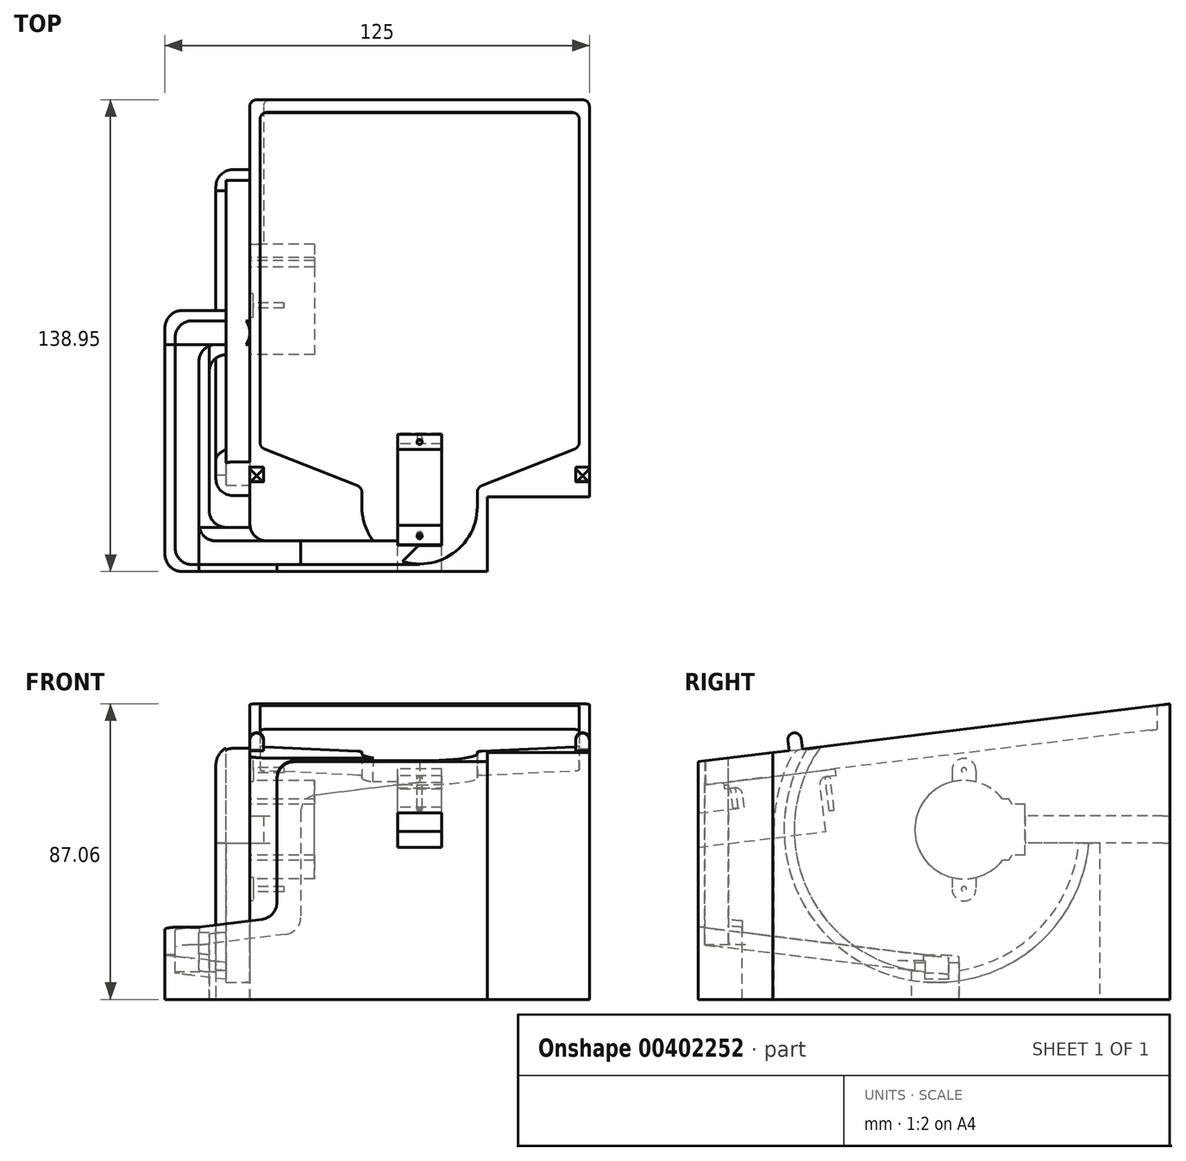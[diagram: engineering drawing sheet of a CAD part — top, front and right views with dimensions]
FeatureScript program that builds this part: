
annotation { "Feature Type Name" : "Feature", "Feature Type Description" : "" }
export const myFeature = defineFeature(function(context is Context, id is Id, definition is map)
    precondition{}
    {
        {
            var Q0;
            Q0=qCreatedBy(makeId("Right.planeOp"),FACE);
            var sketch = newSketch(context, id + "F0", { "sketchPlane" : qUnion([Q0])});
            skLineSegment(sketch, "E0", {"start": v(-65.34, 50) * mm, "end": v(-65.34, -20) * mm});
            skLineSegment(sketch, "E1", {"start": v(-65.34, -20) * mm, "end": v(73.61, -20) * mm});
            skLineSegment(sketch, "E2", {"start": v(73.61, -20) * mm, "end": v(73.61, 67.06) * mm});
            skLineSegment(sketch, "E3", {"start": v(73.61, 67.06) * mm, "end": v(-65.34, 50) * mm});
            skPoint(sketch, "E4", {"position": v(0, 58.02) * mm});
            skPoint(sketch, "E5", {"position": v(0, 50.97) * mm});
            skSolve(sketch);
        }
        {
            var Q0;
            Q0=qSketchRegion(id+"F0",true);
            extrude(context, id + "F1", {"entities" : qUnion([Q0]), "depth" : 50 * mm, "hasSecondDirection" : true, "secondDirectionOppositeDirection" : true, "secondDirectionDepth" : 50 * mm});
        }
        {
            var Q0;
            Q0=makeQuery(id+"F1.opExtrude","SWEPT_FACE",FACE,{"disambiguationData":[OSD([sQuery(id+"F0.wireOp",EDGE,"E3")])]});
            var sketch = newSketch(context, id + "F2", { "sketchPlane" : qUnion([Q0])});
            skPoint(sketch, "E6.endSnap0", {"position": v(0, -57.54) * mm});
            skPoint(sketch, "E6.end.orphan", {"position": v(0, -83) * mm});
            skPoint(sketch, "E7.orphan", {"position": v(-48, -57.54) * mm});
            skPoint(sketch, "E8.orphan", {"position": v(48, -57.54) * mm});
            skLineSegment(sketch, "E9.0", {"start": v(47, 77.46) * mm, "end": v(-47, 77.46) * mm});
            skLineSegment(sketch, "E9.1", {"start": v(47, 77.46) * mm, "end": v(47, -21.86) * mm});
            skLineSegment(sketch, "E9.2", {"start": v(-47, 77.46) * mm, "end": v(-47, -21.86) * mm});
            skLineSegment(sketch, "E9.3", {"start": v(17, -33.86) * mm, "end": v(47, -21.86) * mm});
            skLineSegment(sketch, "E9.4", {"start": v(-17, -33.86) * mm, "end": v(-47, -21.86) * mm});
            skLineSegment(sketch, "E9.5", {"start": v(-17, -39.54) * mm, "end": v(-17, -33.86) * mm});
            skArc(sketch, "E9.6", {"start": v(-17, -39.54) * mm, "mid": v(0, -56.54) * mm, "end": v(17, -39.54) * mm});
            skLineSegment(sketch, "E9.7", {"start": v(17, -39.54) * mm, "end": v(17, -33.86) * mm});
            skPoint(sketch, "E10.bottom.end.orphan", {"position": v(-48, 78.46) * mm});
            skPoint(sketch, "E10.bottom.start.orphan", {"position": v(48, 78.46) * mm});
            skPoint(sketch, "E11", {"position": v(0, 7.07) * mm});
            skSolve(sketch);
        }
        {
            var Q0;
            Q0=makeQuery(id+"F2.imprint","IMPRINT",FACE,{"disambiguationData":[TD([[makeQuery(id+"F2.imprint","IMPRINT",EDGE,{"derivedFrom":sQuery(id+"F2.wireOp",EDGE,"E9.0")}),1.0]])]});
            cPlane(context, id + "F3", {"entities" : qUnion([Q0]), "cplaneType" : CPlaneType.OFFSET, "offset" : 7 * mm, "oppositeDirection" : true, "width" : 150 * mm, "height" : 150 * mm});
        }
        {
            var Q0;
            Q0=qCreatedBy(id+"F3.planeOp",FACE);
            var sketch = newSketch(context, id + "F4", { "sketchPlane" : qUnion([Q0])});
            skPoint(sketch, "E12", {"position": v(0, 6.21) * mm});
            skPoint(sketch, "E13.endSnap0", {"position": v(0, -58.41) * mm});
            skPoint(sketch, "E13.end.orphan", {"position": v(0, -83.88) * mm});
            skPoint(sketch, "E14.orphan", {"position": v(-48, -58.41) * mm});
            skPoint(sketch, "E15.orphan", {"position": v(48, -58.41) * mm});
            skLineSegment(sketch, "E16.0", {"start": v(47, 76.59) * mm, "end": v(-47, 76.59) * mm});
            skLineSegment(sketch, "E16.1", {"start": v(47, 76.59) * mm, "end": v(47, -22.73) * mm});
            skLineSegment(sketch, "E16.2", {"start": v(-47, 76.59) * mm, "end": v(-47, -22.73) * mm});
            skLineSegment(sketch, "E16.3", {"start": v(17, -34.73) * mm, "end": v(47, -22.73) * mm});
            skLineSegment(sketch, "E16.4", {"start": v(-17, -34.73) * mm, "end": v(-47, -22.73) * mm});
            skLineSegment(sketch, "E16.5", {"start": v(-17, -40.41) * mm, "end": v(-17, -34.73) * mm});
            skArc(sketch, "E16.6", {"start": v(-17, -40.41) * mm, "mid": v(0, -57.41) * mm, "end": v(17, -40.41) * mm});
            skLineSegment(sketch, "E16.7", {"start": v(17, -40.41) * mm, "end": v(17, -34.73) * mm});
            skPoint(sketch, "E17.bottom.end.orphan", {"position": v(-48, 77.59) * mm});
            skPoint(sketch, "E17.bottom.start.orphan", {"position": v(48, 77.59) * mm});
            skSolve(sketch);
        }
        {
            var Q1;
            Q1 = qSketchRegion(id + "F2", true);
            var Q2;
            Q2 = qSketchRegion(id + "F4", true);
            loft(context, id + "F5", {"operationType" : NewBodyOperationType.REMOVE, "sheetProfilesArray" : [{ "sheetProfileEntities" : qUnion([Q1]) }, { "sheetProfileEntities" : qUnion([Q2]) }]});
        }
        {
            var Q0;
            Q0=makeQuery(id+"F1.opExtrude","CAP_FACE",FACE,{"disambiguationData":[OSD([sQuery(id+"F0.wireOp",EDGE,"E0"),sQuery(id+"F0.wireOp",EDGE,"E1"),sQuery(id+"F0.wireOp",EDGE,"E2"),sQuery(id+"F0.wireOp",EDGE,"E3")])],"isStart":true});
            var sketch = newSketch(context, id + "F6", { "sketchPlane" : qUnion([Q0])});
            skArc(sketch, "E18", {"start": v(-24.37, 21) * mm, "mid": v(1.5, 30) * mm, "end": v(-24.37, 39) * mm});
            skPoint(sketch, "E19", {"position": v(-5, 30) * mm});
            skLineSegment(sketch, "E20.bottom", {"start": v(-31, 22.5) * mm, "end": v(-27.13, 22.5) * mm});
            skLineSegment(sketch, "E20.top", {"start": v(-31, 37.5) * mm, "end": v(-27.13, 37.5) * mm});
            skLineSegment(sketch, "E20.left", {"start": v(-31, 22.5) * mm, "end": v(-31, 37.5) * mm});
            skArc(sketch, "E21", {"start": v(-26.23, 39) * mm, "mid": v(-26.7, 38.26) * mm, "end": v(-27.13, 37.5) * mm});
            skLineSegment(sketch, "E22.bottom", {"start": v(-26.23, 39) * mm, "end": v(-24.37, 39) * mm});
            skLineSegment(sketch, "E22.top", {"start": v(-26.23, 21) * mm, "end": v(-24.37, 21) * mm});
            skArc(sketch, "E23.trimOffspring", {"start": v(-27.13, 22.5) * mm, "mid": v(-26.7, 21.74) * mm, "end": v(-26.23, 21) * mm});
            skSolve(sketch);
        }
        {
            var Q0;
            Q0 = qSketchRegion(id + "F6", true);
            extrude(context, id + "F7", {"entities" : qUnion([Q0]), "operationType" : NewBodyOperationType.REMOVE, "oppositeDirection" : true, "depth" : 19 * mm});
        }
        {
            var Q0;
            Q0=makeQuery(id+"F1.opExtrude","CAP_FACE",FACE,{"disambiguationData":[OSD([sQuery(id+"F0.wireOp",EDGE,"E0"),sQuery(id+"F0.wireOp",EDGE,"E1"),sQuery(id+"F0.wireOp",EDGE,"E2"),sQuery(id+"F0.wireOp",EDGE,"E3")])],"isStart":true});
            var sketch = newSketch(context, id + "F8", { "sketchPlane" : qUnion([Q0])});
            skLineSegment(sketch, "E24", {"start": v(-13, 47.5) * mm, "end": v(-13, 12.5) * mm});
            skPoint(sketch, "E25", {"position": v(-13, 30) * mm});
            skArc(sketch, "E26.0.startCap", {"start": v(-16.5, 47.5) * mm, "mid": v(-13, 51) * mm, "end": v(-9.5, 47.5) * mm});
            skArc(sketch, "E26.0.endCap", {"start": v(-9.5, 12.5) * mm, "mid": v(-13, 9) * mm, "end": v(-16.5, 12.5) * mm});
            skLineSegment(sketch, "E26.0.left", {"start": v(-9.5, 47.5) * mm, "end": v(-9.5, 12.5) * mm});
            skLineSegment(sketch, "E26.0.right", {"start": v(-16.5, 47.5) * mm, "end": v(-16.5, 12.5) * mm});
            skSolve(sketch);
        }
        {
            var Q0;
            Q0 = qSketchRegion(id + "F8", true);
            extrude(context, id + "F9", {"entities" : qUnion([Q0]), "operationType" : NewBodyOperationType.REMOVE, "oppositeDirection" : true, "depth" : 1 * mm});
        }
        {
            var Q0;
            Q0=makeQuery(id+"F1.opExtrude","CAP_FACE",FACE,{"disambiguationData":[OSD([sQuery(id+"F0.wireOp",EDGE,"E0"),sQuery(id+"F0.wireOp",EDGE,"E1"),sQuery(id+"F0.wireOp",EDGE,"E2"),sQuery(id+"F0.wireOp",EDGE,"E3")])],"isStart":true});
            var sketch = newSketch(context, id + "F10", { "sketchPlane" : qUnion([Q0])});
            skLineSegment(sketch, "E27.bottom", {"start": v(-81, 34) * mm, "end": v(-21, 34) * mm});
            skLineSegment(sketch, "E27.top", {"start": v(-81, 26) * mm, "end": v(-21, 26) * mm});
            skLineSegment(sketch, "E27.left", {"start": v(-81, 34) * mm, "end": v(-81, 26) * mm});
            skLineSegment(sketch, "E27.right", {"start": v(-21, 34) * mm, "end": v(-21, 26) * mm});
            skPoint(sketch, "E27.middle", {"position": v(-51, 30) * mm});
            skSolve(sketch);
        }
        {
            var Q0;
            Q0 = qSketchRegion(id + "F10", true);
            extrude(context, id + "F11", {"entities" : qUnion([Q0]), "operationType" : NewBodyOperationType.REMOVE, "oppositeDirection" : true, "depth" : 4 * mm});
        }
        {
            var Q0;
            Q0=qCreatedBy(makeId("Front.planeOp"),FACE);
            cPlane(context, id + "F12", {"entities" : qUnion([Q0]), "cplaneType" : CPlaneType.OFFSET, "offset" : 5 * mm, "oppositeDirection" : true, "width" : 150 * mm, "height" : 150 * mm});
        }
        {
            var Q0;
            Q0=qCreatedBy(id+"F12.planeOp",FACE);
            var sketch = newSketch(context, id + "F13", { "sketchPlane" : qUnion([Q0])});
            skLineSegment(sketch, "E28", {"start": v(-50, -20) * mm, "end": v(-75, -20) * mm});
            skLineSegment(sketch, "E29", {"start": v(-50, -9.96) * mm, "end": v(-75, -6.9) * mm});
            skLineSegment(sketch, "E30", {"start": v(-75, -20) * mm, "end": v(-75, -6.9) * mm});
            skLineSegment(sketch, "E31", {"start": v(-50, -20) * mm, "end": v(-50, -9.96) * mm});
            skSolve(sketch);
        }
        {
            var Q0;
            Q0 = qSketchRegion(id + "F13", true);
            extrude(context, id + "F14", {"entities" : qUnion([Q0]), "operationType" : NewBodyOperationType.ADD, "depth" : 6.5 * mm, "hasSecondDirection" : true, "secondDirectionOppositeDirection" : true, "secondDirectionDepth" : 6.5 * mm});
        }
        {
            var Q0;
            Q0=makeQuery(id+"F2.imprint","IMPRINT",FACE,{"disambiguationData":[TD([[makeQuery(id+"F2.imprint","IMPRINT",EDGE,{"derivedFrom":sQuery(id+"F2.wireOp",EDGE,"E9.0")}),1.0]])]});
            var sketch = newSketch(context, id + "F15", { "sketchPlane" : qUnion([Q0])});
            skLineSegment(sketch, "E32.bottom", {"start": v(6.5, -46.91) * mm, "end": v(-6.5, -46.91) * mm});
            skLineSegment(sketch, "E32.top", {"start": v(6.5, -23.91) * mm, "end": v(-6.5, -23.91) * mm});
            skLineSegment(sketch, "E32.left", {"start": v(6.5, -46.91) * mm, "end": v(6.5, -23.91) * mm});
            skLineSegment(sketch, "E32.right", {"start": v(-6.5, -46.91) * mm, "end": v(-6.5, -23.91) * mm});
            skPoint(sketch, "E32.middle", {"position": v(0, -35.41) * mm});
            skSolve(sketch);
        }
        {
            var Q0;
            Q0 = qSketchRegion(id + "F15", true);
            extrude(context, id + "F16", {"entities" : qUnion([Q0]), "operationType" : NewBodyOperationType.REMOVE, "oppositeDirection" : true, "depth" : 25 * mm});
        }
        {
            var Q0;
            Q0=makeQuery(id+"F2.imprint","IMPRINT",FACE,{"disambiguationData":[TD([[makeQuery(id+"F2.imprint","IMPRINT",EDGE,{"derivedFrom":sQuery(id+"F2.wireOp",EDGE,"E9.0")}),1.0]])]});
            var sketch = newSketch(context, id + "F17", { "sketchPlane" : qUnion([Q0])});
            skLineSegment(sketch, "E33.bottom", {"start": v(6.5, -18.91) * mm, "end": v(-6.5, -18.91) * mm});
            skLineSegment(sketch, "E33.top", {"start": v(6.5, -51.91) * mm, "end": v(-6.5, -51.91) * mm});
            skLineSegment(sketch, "E33.left", {"start": v(6.5, -18.91) * mm, "end": v(6.5, -51.91) * mm});
            skLineSegment(sketch, "E33.right", {"start": v(-6.5, -18.91) * mm, "end": v(-6.5, -51.91) * mm});
            skPoint(sketch, "E33.middle", {"position": v(0, -35.41) * mm});
            skSolve(sketch);
        }
        {
            var Q0;
            Q0 = qSketchRegion(id + "F17", true);
            extrude(context, id + "F18", {"entities" : qUnion([Q0]), "operationType" : NewBodyOperationType.REMOVE, "oppositeDirection" : true, "depth" : 9 * mm});
        }
        {
            var Q0;
            Q0=makeQuery(id+"FUqeBeKpT4LYNuk_1.boolean.opBoolean","MERGE",FACE,{"derivedFrom":[makeQuery(id+"F1.opExtrude","SWEPT_FACE",FACE,{"disambiguationData":[OSD([sQuery(id+"F0.wireOp",EDGE,"E0")])]}),makeQuery(id+"F61UTTqEWsXgY2D_1.opExtrude","SWEPT_FACE",FACE,{"disambiguationData":[OSD([sQuery(id+"F9Du9WT9e9JY5Dl_1.wireOp",EDGE,"sJgd1tPc-9qsz-vVnT-TqeQ-4TYIqpoZbmCu")])]}),makeQuery(id+"FUqeBeKpT4LYNuk_1.opExtrude","CAP_FACE",FACE,{"disambiguationData":[OSD([sQuery(id+"Fu5qXJoa0auTo1w_1.wireOp",EDGE,"depduNjt-3aMR-BOii-vv3o-0Txvqa5xbjUM"),sQuery(id+"Fu5qXJoa0auTo1w_1.wireOp",EDGE,"YClS0oY7-eXia-WmQ4-NOUT-qmrgQAcRW2ul"),sQuery(id+"Fu5qXJoa0auTo1w_1.wireOp",EDGE,"FjPESpCu-MEkZ-X1k0-rLkk-jPPFp3MV8du9"),sQuery(id+"Fu5qXJoa0auTo1w_1.wireOp",EDGE,"T3NzeVoH-fv4R-7HJz-S144-zwuEIWOQCuFN")])],"isStart":true})]});
            var sketch = newSketch(context, id + "F19", { "sketchPlane" : qUnion([Q0])});
            skLineSegment(sketch, "E34.bottom", {"start": v(50, -20) * mm, "end": v(20, -20) * mm});
            skLineSegment(sketch, "E34.top", {"start": v(50, 60) * mm, "end": v(20, 60) * mm});
            skLineSegment(sketch, "E34.left", {"start": v(50, -20) * mm, "end": v(50, 60) * mm});
            skLineSegment(sketch, "E34.right", {"start": v(20, -20) * mm, "end": v(20, 60) * mm});
            skSolve(sketch);
        }
        {
            var Q0;
            Q0 = qSketchRegion(id + "F19", true);
            extrude(context, id + "F20", {"entities" : qUnion([Q0]), "operationType" : NewBodyOperationType.REMOVE, "oppositeDirection" : true, "depth" : 22 * mm});
        }
        {
            var Q0;
            Q0=makeQuery(id+"F16.boolean.opBoolean","COPY",FACE,{"derivedFrom":makeQuery(id+"F16.opExtrude","SWEPT_FACE",FACE,{"disambiguationData":[OSD([sQuery(id+"F15.wireOp",EDGE,"E32.bottom")])]})});
            var sketch = newSketch(context, id + "F21", { "sketchPlane" : qUnion([Q0])});
            skLineSegment(sketch, "E35.bottom", {"start": v(-6.5, 32.6) * mm, "end": v(6.5, 32.6) * mm});
            skLineSegment(sketch, "E35.top", {"start": v(-6.5, 42.6) * mm, "end": v(6.5, 42.6) * mm});
            skLineSegment(sketch, "E35.left", {"start": v(-6.5, 32.6) * mm, "end": v(-6.5, 42.6) * mm});
            skLineSegment(sketch, "E35.right", {"start": v(6.5, 32.6) * mm, "end": v(6.5, 42.6) * mm});
            skSolve(sketch);
        }
        {
            var Q0;
            Q0 = qSketchRegion(id + "F21", true);
            extrude(context, id + "F22", {"entities" : qUnion([Q0]), "operationType" : NewBodyOperationType.REMOVE, "oppositeDirection" : true, "depth" : 25 * mm});
        }
        {
            var Q0;
            Q0=qCreatedBy(id+"F12.planeOp",FACE);
            var sketch = newSketch(context, id + "F23", { "sketchPlane" : qUnion([Q0])});
            skLineSegment(sketch, "E36", {"start": v(-50, -6.3) * mm, "end": v(-50, -15) * mm});
            skLineSegment(sketch, "E37", {"start": v(-50, -15) * mm, "end": v(-72, -12.3) * mm});
            skLineSegment(sketch, "E38", {"start": v(-72, -12.3) * mm, "end": v(-72, -6.3) * mm});
            skLineSegment(sketch, "E39", {"start": v(-72, -6.3) * mm, "end": v(-50, -6.3) * mm});
            skSolve(sketch);
        }
        {
            var Q0;
            Q0 = qSketchRegion(id + "F23", true);
            extrude(context, id + "F24", {"entities" : qUnion([Q0]), "operationType" : NewBodyOperationType.REMOVE, "oppositeDirection" : true, "depth" : 3.5 * mm, "hasSecondDirection" : true, "secondDirectionOppositeDirection" : false, "secondDirectionDepth" : 3.5 * mm});
        }
        {
            var Q0;
            Q0=makeQuery(id+"F14.opExtrude","SWEPT_FACE",FACE,{"disambiguationData":[OSD([sQuery(id+"F13.wireOp",EDGE,"E30")])]});
            var sketch = newSketch(context, id + "F25", { "sketchPlane" : qUnion([Q0])});
            skLineSegment(sketch, "E40", {"start": v(1.5, -20) * mm, "end": v(65.34, -20) * mm});
            skLineSegment(sketch, "E41", {"start": v(65.34, -20) * mm, "end": v(65.34, 1.31) * mm});
            skLineSegment(sketch, "E42", {"start": v(65.34, 1.31) * mm, "end": v(-1.5, -6.9) * mm});
            skLineSegment(sketch, "E43", {"start": v(-1.5, -6.9) * mm, "end": v(-1.5, -20) * mm});
            skLineSegment(sketch, "E44", {"start": v(-1.5, -20) * mm, "end": v(1.5, -20) * mm});
            skSolve(sketch);
        }
        {
            var Q0;
            Q0 = qSketchRegion(id + "F25", true);
            extrude(context, id + "F26", {"entities" : qUnion([Q0]), "operationType" : NewBodyOperationType.ADD, "oppositeDirection" : true, "depth" : 13 * mm});
        }
        {
            var Q0;
            Q0=makeQuery(id+"F26.boolean.opBoolean","MERGE",FACE,{"derivedFrom":[makeQuery(id+"F14.opExtrude","SWEPT_FACE",FACE,{"disambiguationData":[OSD([sQuery(id+"F13.wireOp",EDGE,"E30")])]}),makeQuery(id+"F26.opExtrude","CAP_FACE",FACE,{"disambiguationData":[OSD([sQuery(id+"F25.wireOp",EDGE,"E40"),sQuery(id+"F25.wireOp",EDGE,"E41"),sQuery(id+"F25.wireOp",EDGE,"E42"),sQuery(id+"F25.wireOp",EDGE,"E43"),sQuery(id+"F25.wireOp",EDGE,"E44")])],"isStart":true})]});
            cPlane(context, id + "F27", {"entities" : qUnion([Q0]), "cplaneType" : CPlaneType.OFFSET, "offset" : 3 * mm, "oppositeDirection" : true, "width" : 150 * mm, "height" : 150 * mm});
        }
        {
            var Q0;
            Q0=qCreatedBy(id+"F27.planeOp",FACE);
            var sketch = newSketch(context, id + "F28", { "sketchPlane" : qUnion([Q0])});
            skLineSegment(sketch, "E45", {"start": v(-1.5, -2.4) * mm, "end": v(-1.5, -11.93) * mm});
            skLineSegment(sketch, "E46", {"start": v(-1.5, -11.93) * mm, "end": v(63.34, -3.97) * mm});
            skLineSegment(sketch, "E47", {"start": v(63.34, -3.97) * mm, "end": v(63.34, 3.33) * mm});
            skLineSegment(sketch, "E48", {"start": v(63.34, 3.33) * mm, "end": v(-1.5, 3.33) * mm});
            skLineSegment(sketch, "E49", {"start": v(-1.5, 3.33) * mm, "end": v(-1.5, -2.4) * mm});
            skSolve(sketch);
        }
        {
            var Q0;
            Q0 = qSketchRegion(id + "F28", true);
            extrude(context, id + "F29", {"entities" : qUnion([Q0]), "operationType" : NewBodyOperationType.REMOVE, "oppositeDirection" : true, "depth" : 7 * mm});
        }
        {
            var Q0;
            Q0=makeQuery(id+"F1.opExtrude","SWEPT_FACE",FACE,{"disambiguationData":[OSD([sQuery(id+"F0.wireOp",EDGE,"E0")])]});
            var sketch = newSketch(context, id + "F30", { "sketchPlane" : qUnion([Q0])});
            skLineSegment(sketch, "E50", {"start": v(-50, -20) * mm, "end": v(-50, 3.16) * mm});
            skLineSegment(sketch, "E51", {"start": v(-50, 3.16) * mm, "end": v(-65, 1.31) * mm});
            skLineSegment(sketch, "E52", {"start": v(-65, 1.31) * mm, "end": v(-65, -20) * mm});
            skLineSegment(sketch, "E53", {"start": v(-65, -20) * mm, "end": v(-50, -20) * mm});
            skSolve(sketch);
        }
        {
            var Q0;
            Q0 = qSketchRegion(id + "F30", true);
            extrude(context, id + "F31", {"entities" : qUnion([Q0]), "operationType" : NewBodyOperationType.ADD, "oppositeDirection" : true, "depth" : 13 * mm});
        }
        {
            var Q0;
            Q0=makeQuery(id+"F29.boolean.opBoolean","COPY",FACE,{"derivedFrom":makeQuery(id+"F29.opExtrude","SWEPT_FACE",FACE,{"disambiguationData":[OSD([sQuery(id+"F28.wireOp",EDGE,"E47")])]})});
            var sketch = newSketch(context, id + "F32", { "sketchPlane" : qUnion([Q0])});
            skLineSegment(sketch, "E54", {"start": v(65, -3.97) * mm, "end": v(65, 76.03) * mm});
            skLineSegment(sketch, "E55", {"start": v(65, 76.03) * mm, "end": v(0, 76.03) * mm});
            skLineSegment(sketch, "E56", {"start": v(0, 76.03) * mm, "end": v(0, 43.93) * mm});
            skLineSegment(sketch, "E57", {"start": v(0, 43.93) * mm, "end": v(35, 39.63) * mm});
            skLineSegment(sketch, "E58", {"start": v(35, 39.63) * mm, "end": v(35, -0.29) * mm});
            skLineSegment(sketch, "E59", {"start": v(35, -0.29) * mm, "end": v(65, -3.97) * mm});
            skSolve(sketch);
        }
        {
            var Q0;
            Q0 = qSketchRegion(id + "F32", true);
            extrude(context, id + "F33", {"entities" : qUnion([Q0]), "operationType" : NewBodyOperationType.REMOVE, "depth" : 7 * mm});
        }
        {
            var Q0;
            Q0=makeQuery(id+"F33.boolean.opBoolean","MERGE",FACE,{"derivedFrom":[makeQuery(id+"F29.boolean.opBoolean","COPY",FACE,{"derivedFrom":makeQuery(id+"F29.opExtrude","SWEPT_FACE",FACE,{"disambiguationData":[OSD([sQuery(id+"F28.wireOp",EDGE,"E47")])]})}),makeQuery(id+"F33.opExtrude","CAP_FACE",FACE,{"disambiguationData":[OSD([sQuery(id+"F32.wireOp",EDGE,"E54"),sQuery(id+"F32.wireOp",EDGE,"E55"),sQuery(id+"F32.wireOp",EDGE,"E56"),sQuery(id+"F32.wireOp",EDGE,"E57"),sQuery(id+"F32.wireOp",EDGE,"E58"),sQuery(id+"F32.wireOp",EDGE,"E59")])],"isStart":true})]});
            var sketch = newSketch(context, id + "F34", { "sketchPlane" : qUnion([Q0])});
            skLineSegment(sketch, "E60", {"start": v(50, 3.16) * mm, "end": v(42, 4.14) * mm});
            skLineSegment(sketch, "E61", {"start": v(42, 4.14) * mm, "end": v(42, 50.25) * mm});
            skLineSegment(sketch, "E62", {"start": v(42, 50.25) * mm, "end": v(50, 50.25) * mm});
            skLineSegment(sketch, "E63", {"start": v(50, 50.25) * mm, "end": v(50, 3.16) * mm});
            skSolve(sketch);
        }
        {
            var Q0;
            Q0 = qSketchRegion(id + "F34", true);
            extrude(context, id + "F35", {"entities" : qUnion([Q0]), "operationType" : NewBodyOperationType.REMOVE, "oppositeDirection" : true, "depth" : 3 * mm});
        }
        {
            var Q0;
            Q0=makeQuery(id+"F6.imprint","IMPRINT",FACE,{"disambiguationData":[TD([[makeQuery(id+"F6.imprint","IMPRINT",EDGE,{"derivedFrom":sQuery(id+"F6.wireOp",EDGE,"E18")}),-1.0]])]});
            var sketch = newSketch(context, id + "F36", { "sketchPlane" : qUnion([Q0])});
            skArc(sketch, "E64", {"start": v(-49.82, 26) * mm, "mid": v(-37.7, -0.92) * mm, "end": v(-11.5, -14.53) * mm});
            skArc(sketch, "E65", {"start": v(43, 30) * mm, "mid": v(41.44, 42.14) * mm, "end": v(36.86, 53.5) * mm});
            skLineSegment(sketch, "E66", {"start": v(36.86, 53.5) * mm, "end": v(33.1, 53.96) * mm});
            skPoint(sketch, "E67", {"position": v(43, 30) * mm});
            skLineSegment(sketch, "E68", {"start": v(43, 30) * mm, "end": v(43, -20) * mm});
            skLineSegment(sketch, "E69", {"start": v(-53, 26) * mm, "end": v(-53, -20) * mm});
            skLineSegment(sketch, "E70", {"start": v(-53, -20) * mm, "end": v(43, -20) * mm});
            skLineSegment(sketch, "E71", {"start": v(-53, 26) * mm, "end": v(-49.82, 26) * mm});
            skLineSegment(sketch, "E72", {"start": v(-11.5, -14.53) * mm, "end": v(-11.5, -20) * mm});
            skLineSegment(sketch, "E73", {"start": v(1.5, -14.53) * mm, "end": v(1.5, -20) * mm});
            skArc(sketch, "E74.trimOffspring", {"start": v(1.5, -14.53) * mm, "mid": v(35.86, 11.15) * mm, "end": v(33.1, 53.96) * mm});
            skSolve(sketch);
        }
        {
            var Q0;
            Q0 = qSketchRegion(id + "F36", true);
            extrude(context, id + "F37", {"entities" : qUnion([Q0]), "operationType" : NewBodyOperationType.ADD, "depth" : 10 * mm});
        }
        {
            var Q0;
            Q0=makeQuery(id+"F37.opExtrude","CAP_FACE",FACE,{"disambiguationData":[OSD([sQuery(id+"F36.wireOp",EDGE,"E64"),sQuery(id+"F36.wireOp",EDGE,"E69"),sQuery(id+"F36.wireOp",EDGE,"E70"),sQuery(id+"F36.wireOp",EDGE,"E71"),sQuery(id+"F36.wireOp",EDGE,"E72")])],"isStart":false});
            var sketch = newSketch(context, id + "F38", { "sketchPlane" : qUnion([Q0])});
            skArc(sketch, "E75", {"start": v(1.5, -14.53) * mm, "mid": v(35.86, 11.15) * mm, "end": v(33.1, 53.96) * mm});
            skArc(sketch, "E76", {"start": v(1.5, -11.5) * mm, "mid": v(33.73, 13.76) * mm, "end": v(29.15, 54.44) * mm});
            skLineSegment(sketch, "E77", {"start": v(-49.82, 26) * mm, "end": v(-46.8, 26) * mm});
            skLineSegment(sketch, "E78", {"start": v(33.1, 53.96) * mm, "end": v(29.15, 54.44) * mm});
            skLineSegment(sketch, "E79", {"start": v(-11.5, -14.53) * mm, "end": v(-11.5, -11.5) * mm});
            skLineSegment(sketch, "E80", {"start": v(1.5, -14.53) * mm, "end": v(1.5, -11.5) * mm});
            skArc(sketch, "E81.trimOffspring", {"start": v(-46.8, 26) * mm, "mid": v(-35.58, 1.2) * mm, "end": v(-11.5, -11.5) * mm});
            skArc(sketch, "E82.trimOffspring", {"start": v(-49.82, 26) * mm, "mid": v(-37.7, -0.92) * mm, "end": v(-11.5, -14.53) * mm});
            skSolve(sketch);
        }
        {
            var Q0;
            Q0 = qSketchRegion(id + "F38", true);
            extrude(context, id + "F39", {"entities" : qUnion([Q0]), "operationType" : NewBodyOperationType.ADD, "oppositeDirection" : true, "depth" : 3 * mm});
        }
        {
            var Q0;
            Q0=makeQuery(id+"F6.imprint","IMPRINT",FACE,{"disambiguationData":[TD([[makeQuery(id+"F6.imprint","IMPRINT",EDGE,{"derivedFrom":sQuery(id+"F6.wireOp",EDGE,"E18")}),-1.0]])]});
            var sketch = newSketch(context, id + "F40", { "sketchPlane" : qUnion([Q0])});
            skCircle(sketch, "E83", {"center": v(-5, 30) * mm, "radius": 45 * mm});
            skSolve(sketch);
        }
        {
            var Q0;
            Q0 = qSketchRegion(id + "F40", true);
            extrude(context, id + "F41", {"entities" : qUnion([Q0]), "operationType" : NewBodyOperationType.REMOVE, "depth" : 7 * mm});
        }
        {
            var Q0;
            Q0=makeQuery(id+"F20.boolean.opBoolean","COPY",EDGE,{"derivedFrom":makeQuery(id+"F20.opExtrude","CAP_EDGE",EDGE,{"disambiguationData":[OSD([sQuery(id+"F19.wireOp",EDGE,"E34.right")])],"isStart":true})});
            var Q1;
            Q1=makeQuery(id+"F20.boolean.opBoolean","COPY",EDGE,{"derivedFrom":makeQuery(id+"F20.opExtrude","CAP_EDGE",EDGE,{"disambiguationData":[OSD([sQuery(id+"F19.wireOp",EDGE,"E34.left")])],"isStart":false})});
            var Q2;
            Q2=makeQuery(id+"F37.opExtrude","CAP_EDGE",EDGE,{"disambiguationData":[OSD([sQuery(id+"F36.wireOp",EDGE,"E69")])],"isStart":false});
            var Q3;
            Q3=makeQuery(id+"F37.opExtrude","CAP_EDGE",EDGE,{"disambiguationData":[OSD([sQuery(id+"F36.wireOp",EDGE,"E68")])],"isStart":false});
            var Q4;
            Q4=makeQuery(id+"F37.opExtrude","SWEPT_EDGE",EDGE,{"disambiguationData":[OSD([sQuery(id+"F0.wireOp",EDGE,"E3"),sQuery(id+"F36.wireOp",EDGE,"E65"),sQuery(id+"F36.wireOp",EDGE,"E66")])]});
            var Q5;
            Q5=makeQuery(id+"F39.boolean.opBoolean","MERGE",EDGE,{"derivedFrom":[makeQuery(id+"F37.opExtrude","CAP_EDGE",EDGE,{"disambiguationData":[OSD([sQuery(id+"F36.wireOp",EDGE,"E66")])],"isStart":false}),makeQuery(id+"F39.opExtrude","CAP_EDGE",EDGE,{"disambiguationData":[OSD([sQuery(id+"F38.wireOp",EDGE,"E78")])],"isStart":true})]});
            var Q6;
            Q6=makeQuery(id+"F14.opExtrude","CAP_EDGE",EDGE,{"disambiguationData":[OSD([sQuery(id+"F13.wireOp",EDGE,"E30")])],"isStart":true});
            var Q7;
            Q7=makeQuery(id+"F26.opExtrude","CAP_EDGE",EDGE,{"disambiguationData":[OSD([sQuery(id+"F25.wireOp",EDGE,"E41")])],"isStart":true});
            var Q8;
            Q8=makeQuery(id+"F35.boolean.opBoolean","INTERSECT",EDGE,{"derivedFrom":[makeQuery(id+"F1.opExtrude","SWEPT_FACE",FACE,{"disambiguationData":[OSD([sQuery(id+"F0.wireOp",EDGE,"E3")])]}),makeQuery(id+"F35.opExtrude","SWEPT_FACE",FACE,{"disambiguationData":[OSD([sQuery(id+"F34.wireOp",EDGE,"E61")])]})]});
            var Q9;
            Q9=makeQuery(id+"F33.boolean.opBoolean","COPY",EDGE,{"derivedFrom":makeQuery(id+"F33.opExtrude","CAP_EDGE",EDGE,{"disambiguationData":[OSD([sQuery(id+"F32.wireOp",EDGE,"E54")])],"isStart":false})});
            var Q10;
            Q10=makeQuery(id+"F31.boolean.opBoolean","INTERSECT",EDGE,{"derivedFrom":[makeQuery(id+"F26.opExtrude","CAP_FACE",FACE,{"disambiguationData":[OSD([sQuery(id+"F25.wireOp",EDGE,"E40"),sQuery(id+"F25.wireOp",EDGE,"E41"),sQuery(id+"F25.wireOp",EDGE,"E42"),sQuery(id+"F25.wireOp",EDGE,"E43"),sQuery(id+"F25.wireOp",EDGE,"E44")])],"isStart":false}),makeQuery(id+"F31.opExtrude","CAP_FACE",FACE,{"disambiguationData":[OSD([sQuery(id+"F30.wireOp",EDGE,"E50"),sQuery(id+"F30.wireOp",EDGE,"E51"),sQuery(id+"F30.wireOp",EDGE,"E52"),sQuery(id+"F30.wireOp",EDGE,"E53")])],"isStart":false})]});
            var Q11;
            Q11=makeQuery(id+"F29.boolean.opBoolean","COPY",EDGE,{"derivedFrom":makeQuery(id+"F29.opExtrude","CAP_EDGE",EDGE,{"disambiguationData":[OSD([sQuery(id+"F28.wireOp",EDGE,"E47")])],"isStart":true})});
            var Q12;
            Q12=makeQuery(id+"F26.boolean.opBoolean","INTERSECT",EDGE,{"derivedFrom":[makeQuery(id+"F14.opExtrude","CAP_FACE",FACE,{"disambiguationData":[OSD([sQuery(id+"F13.wireOp",EDGE,"E28"),sQuery(id+"F13.wireOp",EDGE,"E29"),sQuery(id+"F13.wireOp",EDGE,"E30"),sQuery(id+"F13.wireOp",EDGE,"E31")])],"isStart":false}),makeQuery(id+"F26.opExtrude","CAP_FACE",FACE,{"disambiguationData":[OSD([sQuery(id+"F25.wireOp",EDGE,"E40"),sQuery(id+"F25.wireOp",EDGE,"E41"),sQuery(id+"F25.wireOp",EDGE,"E42"),sQuery(id+"F25.wireOp",EDGE,"E43"),sQuery(id+"F25.wireOp",EDGE,"E44")])],"isStart":false})]});
            var Q13;
            Q13=makeQuery(id+"F24.boolean.opBoolean","COPY",EDGE,{"derivedFrom":makeQuery(id+"F24.opExtrude","CAP_EDGE",EDGE,{"disambiguationData":[OSD([sQuery(id+"F23.wireOp",EDGE,"E38")])],"isStart":false})});
            var Q14;
            Q14=makeQuery(id+"F29.boolean.opBoolean","COPY",EDGE,{"derivedFrom":makeQuery(id+"F29.opExtrude","CAP_EDGE",EDGE,{"disambiguationData":[OSD([sQuery(id+"F28.wireOp",EDGE,"E45"),sQuery(id+"F28.wireOp",EDGE,"E49")])],"isStart":false})});
            var Q15;
            Q15=makeQuery(id+"F35.boolean.opBoolean","COPY",EDGE,{"derivedFrom":makeQuery(id+"F35.opExtrude","SWEPT_EDGE",EDGE,{"disambiguationData":[OSD([sQuery(id+"F34.wireOp",EDGE,"E60"),sQuery(id+"F34.wireOp",EDGE,"E61")])]})});
            var Q16;
            Q16=makeQuery(id+"F33.boolean.opBoolean","COPY",EDGE,{"derivedFrom":makeQuery(id+"F33.opExtrude","SWEPT_EDGE",EDGE,{"disambiguationData":[OSD([sQuery(id+"F32.wireOp",EDGE,"E58"),sQuery(id+"F32.wireOp",EDGE,"E59")])]})});
            var Q17;
            Q17=makeQuery(id+"F33.boolean.opBoolean","COPY",EDGE,{"derivedFrom":makeQuery(id+"F33.opExtrude","SWEPT_EDGE",EDGE,{"disambiguationData":[OSD([sQuery(id+"F32.wireOp",EDGE,"E57"),sQuery(id+"F32.wireOp",EDGE,"E58")])]})});
            var Q18;
            Q18=makeQuery(id+"F33.boolean.opBoolean","INTERSECT",EDGE,{"derivedFrom":[makeQuery(id+"F24.boolean.opBoolean","MERGE",FACE,{"derivedFrom":[makeQuery(id+"F1.opExtrude","CAP_FACE",FACE,{"disambiguationData":[OSD([sQuery(id+"F0.wireOp",EDGE,"E0"),sQuery(id+"F0.wireOp",EDGE,"E1"),sQuery(id+"F0.wireOp",EDGE,"E2"),sQuery(id+"F0.wireOp",EDGE,"E3")])],"isStart":true}),makeQuery(id+"F24.opExtrude","SWEPT_FACE",FACE,{"disambiguationData":[OSD([sQuery(id+"F23.wireOp",EDGE,"E36")])]})]}),makeQuery(id+"F33.opExtrude","CAP_FACE",FACE,{"disambiguationData":[OSD([sQuery(id+"F32.wireOp",EDGE,"E54"),sQuery(id+"F32.wireOp",EDGE,"E55"),sQuery(id+"F32.wireOp",EDGE,"E56"),sQuery(id+"F32.wireOp",EDGE,"E57"),sQuery(id+"F32.wireOp",EDGE,"E58"),sQuery(id+"F32.wireOp",EDGE,"E59")])],"isStart":false})]});
            fillet(context, id + "F42", {"entities" : qUnion([Q0, Q1, Q2, Q3, Q4, Q5, Q6, Q7, Q8, Q9, Q10, Q11, Q12, Q13, Q14, Q15, Q16, Q17, Q18]), "radius" : 5 * mm, "tangentPropagation" : true, "allowEdgeOverflow" : false});
        }
        {
            var Q0;
            Q0=makeQuery(id+"F5.boolean.opBoolean","COPY",EDGE,{"derivedFrom":makeQuery(id+"F5.opLoft","SWEPT_EDGE",EDGE,{"disambiguationData":[OSD([sQuery(id+"F2.wireOp",EDGE,"E9.0"),sQuery(id+"F2.wireOp",EDGE,"E9.2"),sQuery(id+"F4.wireOp",EDGE,"E16.0"),sQuery(id+"F4.wireOp",EDGE,"E16.2")])]})});
            var Q1;
            Q1=makeQuery(id+"F5.boolean.opBoolean","COPY",EDGE,{"derivedFrom":makeQuery(id+"F5.opLoft","SWEPT_EDGE",EDGE,{"disambiguationData":[OSD([sQuery(id+"F2.wireOp",EDGE,"E9.0"),sQuery(id+"F2.wireOp",EDGE,"E9.1"),sQuery(id+"F4.wireOp",EDGE,"E16.0"),sQuery(id+"F4.wireOp",EDGE,"E16.1")])]})});
            var Q2;
            Q2=makeQuery(id+"F5.boolean.opBoolean","COPY",EDGE,{"derivedFrom":makeQuery(id+"F5.opLoft","SWEPT_EDGE",EDGE,{"disambiguationData":[OSD([sQuery(id+"F2.wireOp",EDGE,"E9.2"),sQuery(id+"F2.wireOp",EDGE,"E9.4"),sQuery(id+"F4.wireOp",EDGE,"E16.2"),sQuery(id+"F4.wireOp",EDGE,"E16.4")])]})});
            var Q3;
            Q3=makeQuery(id+"F5.boolean.opBoolean","COPY",EDGE,{"derivedFrom":makeQuery(id+"F5.opLoft","SWEPT_EDGE",EDGE,{"disambiguationData":[OSD([sQuery(id+"F2.wireOp",EDGE,"E9.1"),sQuery(id+"F2.wireOp",EDGE,"E9.3"),sQuery(id+"F4.wireOp",EDGE,"E16.1"),sQuery(id+"F4.wireOp",EDGE,"E16.3")])]})});
            var Q4;
            Q4=makeQuery(id+"F5.boolean.opBoolean","COPY",EDGE,{"derivedFrom":makeQuery(id+"F5.opLoft","SWEPT_EDGE",EDGE,{"disambiguationData":[OSD([sQuery(id+"F2.wireOp",EDGE,"E9.3"),sQuery(id+"F2.wireOp",EDGE,"E9.7"),sQuery(id+"F4.wireOp",EDGE,"E16.3"),sQuery(id+"F4.wireOp",EDGE,"E16.7")])]})});
            var Q5;
            Q5=makeQuery(id+"F5.boolean.opBoolean","COPY",EDGE,{"derivedFrom":makeQuery(id+"F5.opLoft","SWEPT_EDGE",EDGE,{"disambiguationData":[OSD([sQuery(id+"F2.wireOp",EDGE,"E9.4"),sQuery(id+"F2.wireOp",EDGE,"E9.5"),sQuery(id+"F4.wireOp",EDGE,"E16.4"),sQuery(id+"F4.wireOp",EDGE,"E16.5")])]})});
            var Q6;
            {var subQ0=sQuery(id+"F6.wireOp",EDGE,"E18");Q6=makeQuery(id+"F9.boolean.opBoolean","SPLIT",EDGE,{"disambiguationData":[TD([makeQuery(id+"F7.boolean.opBoolean","COPY",FACE,{"derivedFrom":makeQuery(id+"F7.opExtrude","SWEPT_FACE",FACE,{"disambiguationData":[OSD([sQuery(id+"F6.wireOp",EDGE,"E22.bottom")])]})})])],"derivedFrom":makeQuery(id+"F7.boolean.opBoolean","COPY",EDGE,{"derivedFrom":makeQuery(id+"F7.opExtrude","CAP_EDGE",EDGE,{"disambiguationData":[OSD([subQ0])],"isStart":true})})});}
            var Q7;
            Q7=makeQuery(id+"F7.boolean.opBoolean","COPY",EDGE,{"derivedFrom":makeQuery(id+"F7.opExtrude","CAP_EDGE",EDGE,{"disambiguationData":[OSD([sQuery(id+"F6.wireOp",EDGE,"E20.bottom")])],"isStart":true})});
            var Q8;
            Q8=makeQuery(id+"F7.boolean.opBoolean","COPY",EDGE,{"derivedFrom":makeQuery(id+"F7.opExtrude","CAP_EDGE",EDGE,{"disambiguationData":[OSD([sQuery(id+"F6.wireOp",EDGE,"E20.top")])],"isStart":true})});
            var Q9;
            {var subQ0=sQuery(id+"F6.wireOp",EDGE,"E20.left");Q9=makeQuery(id+"F11.boolean.opBoolean","SPLIT",EDGE,{"disambiguationData":[TD([makeQuery(id+"F7.boolean.opBoolean","COPY",FACE,{"derivedFrom":makeQuery(id+"F7.opExtrude","SWEPT_FACE",FACE,{"disambiguationData":[OSD([sQuery(id+"F6.wireOp",EDGE,"E20.top")])]})})])],"derivedFrom":makeQuery(id+"F7.boolean.opBoolean","COPY",EDGE,{"derivedFrom":makeQuery(id+"F7.opExtrude","CAP_EDGE",EDGE,{"disambiguationData":[OSD([subQ0])],"isStart":true})})});}
            var Q10;
            {var subQ0=sQuery(id+"F6.wireOp",EDGE,"E20.left");Q10=makeQuery(id+"F11.boolean.opBoolean","SPLIT",EDGE,{"disambiguationData":[TD([makeQuery(id+"F7.boolean.opBoolean","COPY",FACE,{"derivedFrom":makeQuery(id+"F7.opExtrude","SWEPT_FACE",FACE,{"disambiguationData":[OSD([sQuery(id+"F6.wireOp",EDGE,"E20.bottom")])]})})])],"derivedFrom":makeQuery(id+"F7.boolean.opBoolean","COPY",EDGE,{"derivedFrom":makeQuery(id+"F7.opExtrude","CAP_EDGE",EDGE,{"disambiguationData":[OSD([subQ0])],"isStart":true})})});}
            var Q11;
            Q11=makeQuery(id+"F18.boolean.opBoolean","INTERSECT",EDGE,{"derivedFrom":[makeQuery(id+"F16.boolean.opBoolean","COPY",FACE,{"derivedFrom":makeQuery(id+"F16.opExtrude","SWEPT_FACE",FACE,{"disambiguationData":[OSD([sQuery(id+"F15.wireOp",EDGE,"E32.top")])]})}),makeQuery(id+"F18.opExtrude","CAP_FACE",FACE,{"disambiguationData":[OSD([sQuery(id+"F17.wireOp",EDGE,"E33.bottom"),sQuery(id+"F17.wireOp",EDGE,"E33.top"),sQuery(id+"F17.wireOp",EDGE,"E33.left"),sQuery(id+"F17.wireOp",EDGE,"E33.right")])],"isStart":false})]});
            var Q12;
            Q12=makeQuery(id+"F18.boolean.opBoolean","INTERSECT",EDGE,{"derivedFrom":[makeQuery(id+"F16.boolean.opBoolean","COPY",FACE,{"derivedFrom":makeQuery(id+"F16.opExtrude","SWEPT_FACE",FACE,{"disambiguationData":[OSD([sQuery(id+"F15.wireOp",EDGE,"E32.bottom")])]})}),makeQuery(id+"F18.opExtrude","CAP_FACE",FACE,{"disambiguationData":[OSD([sQuery(id+"F17.wireOp",EDGE,"E33.bottom"),sQuery(id+"F17.wireOp",EDGE,"E33.top"),sQuery(id+"F17.wireOp",EDGE,"E33.left"),sQuery(id+"F17.wireOp",EDGE,"E33.right")])],"isStart":false})]});
            var Q13;
            Q13=makeQuery(id+"F1.opExtrude","CAP_EDGE",EDGE,{"disambiguationData":[OSD([sQuery(id+"F0.wireOp",EDGE,"E2")])],"isStart":false});
            var Q14;
            {var subQ0=sQuery(id+"F0.wireOp",EDGE,"E2");var subQ1=sQuery(id+"F0.wireOp",EDGE,"E1");Q14=makeQuery(id+"F11.boolean.opBoolean","SPLIT",EDGE,{"disambiguationData":[TD([makeQuery(id+"F1.opExtrude","SWEPT_FACE",FACE,{"disambiguationData":[OSD([subQ1])]})])],"derivedFrom":makeQuery(id+"F1.opExtrude","CAP_EDGE",EDGE,{"disambiguationData":[OSD([subQ0])],"isStart":true})});}
            var Q15;
            {var subQ0=sQuery(id+"F0.wireOp",EDGE,"E3");var subQ1=sQuery(id+"F0.wireOp",EDGE,"E2");Q15=makeQuery(id+"F11.boolean.opBoolean","SPLIT",EDGE,{"disambiguationData":[TD([makeQuery(id+"F1.opExtrude","SWEPT_FACE",FACE,{"disambiguationData":[OSD([subQ0])]})])],"derivedFrom":makeQuery(id+"F1.opExtrude","CAP_EDGE",EDGE,{"disambiguationData":[OSD([subQ1])],"isStart":true})});}
            var Q16;
            Q16=makeQuery(id+"F11.boolean.opBoolean","INTERSECT",EDGE,{"derivedFrom":[makeQuery(id+"F1.opExtrude","SWEPT_FACE",FACE,{"disambiguationData":[OSD([sQuery(id+"F0.wireOp",EDGE,"E2")])]}),makeQuery(id+"F11.opExtrude","CAP_FACE",FACE,{"disambiguationData":[OSD([sQuery(id+"F10.wireOp",EDGE,"E27.bottom"),sQuery(id+"F10.wireOp",EDGE,"E27.top"),sQuery(id+"F10.wireOp",EDGE,"E27.left"),sQuery(id+"F10.wireOp",EDGE,"E27.right")])],"isStart":false})]});
            var Q17;
            Q17=makeQuery(id+"F41.boolean.opBoolean","MERGE",EDGE,{"derivedFrom":[makeQuery(id+"F39.opExtrude","CAP_EDGE",EDGE,{"disambiguationData":[OSD([sQuery(id+"F38.wireOp",EDGE,"E75")])],"isStart":false}),makeQuery(id+"F39.opExtrude","CAP_EDGE",EDGE,{"disambiguationData":[OSD([sQuery(id+"F38.wireOp",EDGE,"E82.trimOffspring")])],"isStart":false}),makeQuery(id+"F41.opExtrude","CAP_EDGE",EDGE,{"disambiguationData":[OSD([sQuery(id+"F40.wireOp",EDGE,"E83")])],"isStart":false})]});
            fillet(context, id + "F43", {"entities" : qUnion([Q0, Q1, Q2, Q3, Q4, Q5, Q6, Q7, Q8, Q9, Q10, Q11, Q12, Q13, Q14, Q15, Q16, Q17]), "radius" : 2 * mm, "tangentPropagation" : true, "allowEdgeOverflow" : false});
        }
        {
            var Q0;
            Q0=makeQuery(id+"F39.boolean.opBoolean","MERGE",FACE,{"derivedFrom":[makeQuery(id+"F37.boolean.opBoolean","MERGE",FACE,{"derivedFrom":[makeQuery(id+"F1.opExtrude","SWEPT_FACE",FACE,{"disambiguationData":[OSD([sQuery(id+"F0.wireOp",EDGE,"E3")])]}),makeQuery(id+"F37.opExtrude","SWEPT_FACE",FACE,{"disambiguationData":[OSD([sQuery(id+"F36.wireOp",EDGE,"E66")])]})]}),makeQuery(id+"F39.opExtrude","SWEPT_FACE",FACE,{"disambiguationData":[OSD([sQuery(id+"F38.wireOp",EDGE,"E78")])]})]});
            var sketch = newSketch(context, id + "F44", { "sketchPlane" : qUnion([Q0])});
            skLineSegment(sketch, "E84.bottom", {"start": v(50, -31.76) * mm, "end": v(46, -31.76) * mm});
            skLineSegment(sketch, "E84.top", {"start": v(50, -27.76) * mm, "end": v(46, -27.76) * mm});
            skLineSegment(sketch, "E84.left", {"start": v(50, -31.76) * mm, "end": v(50, -27.76) * mm});
            skLineSegment(sketch, "E84.right", {"start": v(46, -31.76) * mm, "end": v(46, -27.76) * mm});
            skLineSegment(sketch, "E85.MirrorCS", {"start": v(-50, -27.76) * mm, "end": v(-46, -27.76) * mm});
            skLineSegment(sketch, "E86.MirrorCS", {"start": v(-46, -31.76) * mm, "end": v(-46, -27.76) * mm});
            skLineSegment(sketch, "E87.MirrorCS", {"start": v(-50, -31.76) * mm, "end": v(-46, -31.76) * mm});
            skLineSegment(sketch, "E88.MirrorCS", {"start": v(-50, -31.76) * mm, "end": v(-50, -27.76) * mm});
            skSolve(sketch);
        }
        {
            var Q0;
            Q0 = qSketchRegion(id + "F44", true);
            extrude(context, id + "F45", {"entities" : qUnion([Q0]), "operationType" : NewBodyOperationType.ADD, "depth" : 5 * mm});
        }
        {
            var Q0;
            Q0=makeQuery(id+"F45.opExtrude","CAP_EDGE",EDGE,{"disambiguationData":[OSD([sQuery(id+"F44.wireOp",EDGE,"E87.MirrorCS")])],"isStart":false});
            var Q1;
            Q1=makeQuery(id+"F45.opExtrude","CAP_EDGE",EDGE,{"disambiguationData":[OSD([sQuery(id+"F44.wireOp",EDGE,"E86.MirrorCS")])],"isStart":false});
            var Q2;
            Q2=makeQuery(id+"F45.opExtrude","CAP_EDGE",EDGE,{"disambiguationData":[OSD([sQuery(id+"F44.wireOp",EDGE,"E88.MirrorCS")])],"isStart":false});
            var Q3;
            Q3=makeQuery(id+"F45.opExtrude","CAP_EDGE",EDGE,{"disambiguationData":[OSD([sQuery(id+"F44.wireOp",EDGE,"E85.MirrorCS")])],"isStart":false});
            var Q4;
            Q4=makeQuery(id+"F45.opExtrude","CAP_EDGE",EDGE,{"disambiguationData":[OSD([sQuery(id+"F44.wireOp",EDGE,"E84.left")])],"isStart":false});
            var Q5;
            Q5=makeQuery(id+"F45.opExtrude","CAP_EDGE",EDGE,{"disambiguationData":[OSD([sQuery(id+"F44.wireOp",EDGE,"E84.bottom")])],"isStart":false});
            var Q6;
            Q6=makeQuery(id+"F45.opExtrude","CAP_EDGE",EDGE,{"disambiguationData":[OSD([sQuery(id+"F44.wireOp",EDGE,"E84.right")])],"isStart":false});
            var Q7;
            Q7=makeQuery(id+"F45.opExtrude","CAP_EDGE",EDGE,{"disambiguationData":[OSD([sQuery(id+"F44.wireOp",EDGE,"E84.top")])],"isStart":false});
            fillet(context, id + "F46", {"entities" : qUnion([Q0, Q1, Q2, Q3, Q4, Q5, Q6, Q7]), "radius" : 2 * mm, "tangentPropagation" : true, "allowEdgeOverflow" : false});
        }
        {
            var Q0;
            {var subQ4=sQuery(id+"F8.wireOp",EDGE,"E26.0.startCap");Q0=makeQuery(id+"F8.imprint","IMPRINT",FACE,{"disambiguationData":[TD([[makeQuery(id+"F8.imprint","IMPRINT",EDGE,{"derivedFrom":subQ4}),-1.0]])]});}
            var sketch = newSketch(context, id + "F47", { "sketchPlane" : qUnion([Q0])});
            skCircle(sketch, "E89", {"center": v(-13, 47.5) * mm, "radius": 0.75 * mm});
            skCircle(sketch, "E90", {"center": v(-13, 12.5) * mm, "radius": 0.75 * mm});
            skSolve(sketch);
        }
        {
            var Q0;
            Q0 = qSketchRegion(id + "F47", true);
            extrude(context, id + "F48", {"entities" : qUnion([Q0]), "operationType" : NewBodyOperationType.REMOVE, "oppositeDirection" : true, "depth" : 10 * mm});
        }
        {
            var Q0;
            {var subQ0=sQuery(id+"F17.wireOp",EDGE,"E33.bottom");var subQ1=sQuery(id+"F17.wireOp",EDGE,"E33.left");var subQ2=sQuery(id+"F17.wireOp",EDGE,"E33.right");Q0=makeQuery(id+"F18.boolean.opBoolean","COPY",FACE,{"disambiguationData":[TD([makeQuery(id+"F16.boolean.opBoolean","COPY",FACE,{"derivedFrom":makeQuery(id+"F16.opExtrude","SWEPT_FACE",FACE,{"disambiguationData":[OSD([sQuery(id+"F15.wireOp",EDGE,"E32.top")])]})})])],"derivedFrom":makeQuery(id+"F18.opExtrude","CAP_FACE",FACE,{"disambiguationData":[OSD([subQ0,sQuery(id+"F17.wireOp",EDGE,"E33.top"),subQ1,subQ2])],"isStart":false})});}
            var sketch = newSketch(context, id + "F49", { "sketchPlane" : qUnion([Q0])});
            skCircle(sketch, "E91", {"center": v(0, -21.41) * mm, "radius": 0.75 * mm});
            skPoint(sketch, "E92", {"position": v(0, -35.41) * mm});
            skCircle(sketch, "E93", {"center": v(0, -49.41) * mm, "radius": 0.75 * mm});
            skPoint(sketch, "E94.orphan", {"position": v(6.5, -21.91) * mm});
            skPoint(sketch, "E95.end.orphan", {"position": v(6.5, -48.91) * mm});
            skPoint(sketch, "E96.end.orphan", {"position": v(-6.5, -48.91) * mm});
            skSolve(sketch);
        }
        {
            var Q0;
            Q0 = qSketchRegion(id + "F49", true);
            extrude(context, id + "F50", {"entities" : qUnion([Q0]), "operationType" : NewBodyOperationType.REMOVE, "oppositeDirection" : true, "depth" : 10 * mm});
        }
    });
